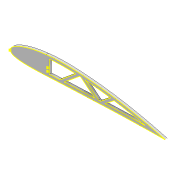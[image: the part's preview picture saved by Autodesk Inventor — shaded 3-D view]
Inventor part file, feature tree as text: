
AUTODESK INVENTOR PART (.ipt)
format: ipt  version: 2022 (Build 260153000, 153)  size: 283,136 bytes
history: native  units: mm
features: sketch x7, extrude x6, projected_geometry x4, shell x1
ambient origin geometry x8: Origin, YZ Plane, XZ Plane, XY Plane, X Axis, Y Axis, Z Axis, Center Point
bodies: Solid1 (feature_tree)
feature tree (18):
  extrude  "Extrusion1"  Depth=5.0mm
  shell  "Shell1"  Thickness=6.0mm
  extrude  "Extrusion2"  Depth=2.0mm
  extrude  "Extrusion3"  Depth=5.9mm
  extrude  "Extrusion4"  Depth=10.0mm TaperAngle=0.0deg
  extrude  "Extrusion5"  Depth=10.0mm TaperAngle=0.0deg
  extrude  "Extrusion7"  Depth=5.0mm
  sketch  "Sketch15"  dims[d20=5.0mm d22=4.5mm d23=0.0mm d24=2.0mm d26=2.0mm d29=4.5mm d30=0.0mm]
  sketch  "Sketch3"  dims[d0=4.5mm d1=0.0mm d2=5.0mm d3=6.0mm]
  sketch  "Sketch7"  dims[d5=4.5mm d6=0.0mm d7=2.0mm]
  projected_geometry  "Projected Loop3"
  sketch  "Sketch8"  dims[d8=2.0mm d9=5.9mm]
  sketch  "Sketch9"  dims[d12=4.0mm d13=10.0mm d14=0.0mm]
  sketch  "Sketch10"  dims[d15=70.0mm d16=10.0mm d17=0.0mm]
  projected_geometry  "Projected Loop4"
  sketch  "Sketch14"  dims[d18=5.0mm d19=5.0mm]
  projected_geometry  "Projected Loop7"
  projected_geometry  "Projected Loop8"
